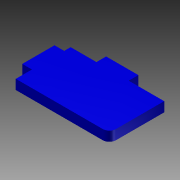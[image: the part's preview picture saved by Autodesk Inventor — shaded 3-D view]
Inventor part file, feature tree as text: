
AUTODESK INVENTOR PART (.ipt)
format: ipt  version: 2012 (Build 160160000, 160)  size: 90,624 bytes
history: native  units: mm
features: extrude x1, sketch x1
ambient origin geometry x8: Origin, YZ Plane, XZ Plane, XY Plane, X Axis, Y Axis, Z Axis, Center Point
bodies: Solid1 (feature_tree)
feature tree (2):
  extrude  "Extrusion1"  Depth=10.0mm
  sketch  "Sketch1"  dims[d4=7.5mm d8=10.0mm d10=3.0mm d13=3.0mm d14=0.0mm d15=2.0mm d16=10.0mm d25=3.0mm d26=5.0mm d33=17.0mm d35=11.0mm d36=11.0mm d38=2.0mm d39=8.0mm d40=32.0mm d41=3.0mm]
